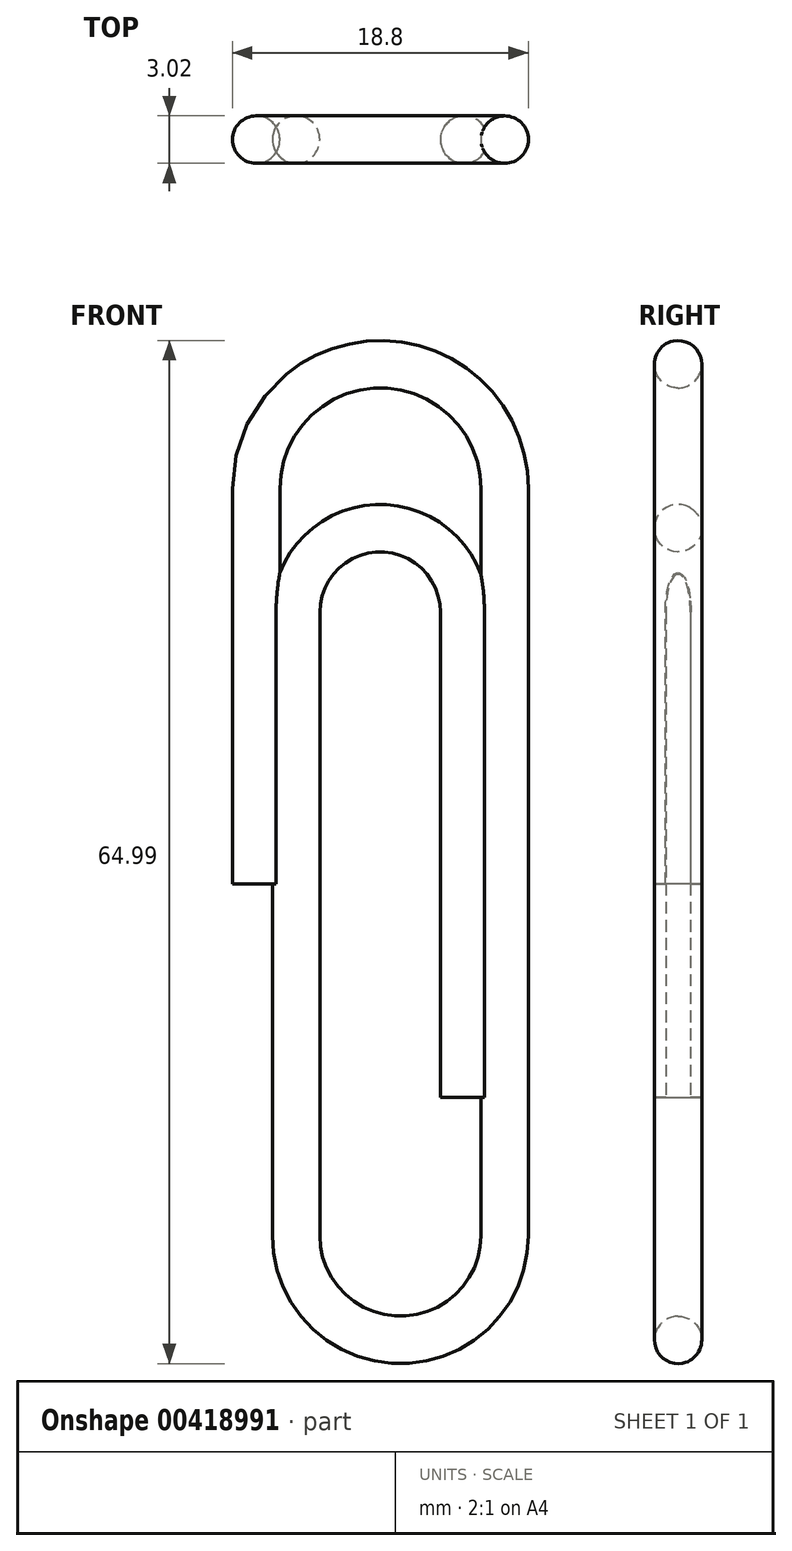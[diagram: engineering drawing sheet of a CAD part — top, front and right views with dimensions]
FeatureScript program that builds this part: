
annotation { "Feature Type Name" : "Feature", "Feature Type Description" : "" }
export const myFeature = defineFeature(function(context is Context, id is Id, definition is map)
    precondition{}
    {
        {
            var Q0;
            Q0=qCreatedBy(makeId("Top.planeOp"),FACE);
            var sketch = newSketch(context, id + "F0", { "sketchPlane" : qUnion([Q0])});
            skCircle(sketch, "E0", {"center": v(0, 0) * mm, "radius": 1.5 * mm});
            skSolve(sketch);
        }
        {
            var Q0;
            Q0=qCreatedBy(makeId("Front.planeOp"),FACE);
            var sketch = newSketch(context, id + "F1", { "sketchPlane" : qUnion([Q0])});
            skLineSegment(sketch, "E1", {"start": v(0, 0) * mm, "end": v(0, 25.13) * mm});
            skArc(sketch, "E2", {"start": v(15.79, 25.13) * mm, "mid": v(7.9, 33.02) * mm, "end": v(0, 25.13) * mm});
            skLineSegment(sketch, "E3", {"start": v(15.79, 25.13) * mm, "end": v(15.79, -22.33) * mm});
            skArc(sketch, "E4", {"start": v(2.54, -22.33) * mm, "mid": v(9.16, -28.95) * mm, "end": v(15.79, -22.33) * mm});
            skLineSegment(sketch, "E5", {"start": v(2.54, -22.33) * mm, "end": v(2.54, 17.28) * mm});
            skArc(sketch, "E6", {"start": v(13.2, 17.28) * mm, "mid": v(7.87, 22.61) * mm, "end": v(2.54, 17.28) * mm});
            skLineSegment(sketch, "E7", {"start": v(13.2, 17.28) * mm, "end": v(13.2, -13.55) * mm});
            skSolve(sketch);
        }
        {
            var Q0;
            Q0=makeQuery(id+"F0.imprint","IMPRINT",FACE,{"disambiguationData":[TD([[makeQuery(id+"F0.imprint","IMPRINT",EDGE,{"derivedFrom":sQuery(id+"F0.wireOp",EDGE,"E0")}),1.0]])]});
            var Q1;
            Q1=sQuery(id+"F1.wireOp",EDGE,"E1");
            var Q2;
            Q2=sQuery(id+"F1.wireOp",EDGE,"E2");
            var Q3;
            Q3=sQuery(id+"F1.wireOp",EDGE,"E3");
            var Q4;
            Q4=sQuery(id+"F1.wireOp",EDGE,"E4");
            var Q5;
            Q5=sQuery(id+"F1.wireOp",EDGE,"E5");
            var Q6;
            Q6=sQuery(id+"F1.wireOp",EDGE,"E6");
            var Q7;
            Q7=sQuery(id+"F1.wireOp",EDGE,"E7");
            sweep(context, id + "F2", {"profiles" : qUnion([Q0]), "path" : qUnion([Q1, Q2, Q3, Q4, Q5, Q6, Q7])});
        }
    });
